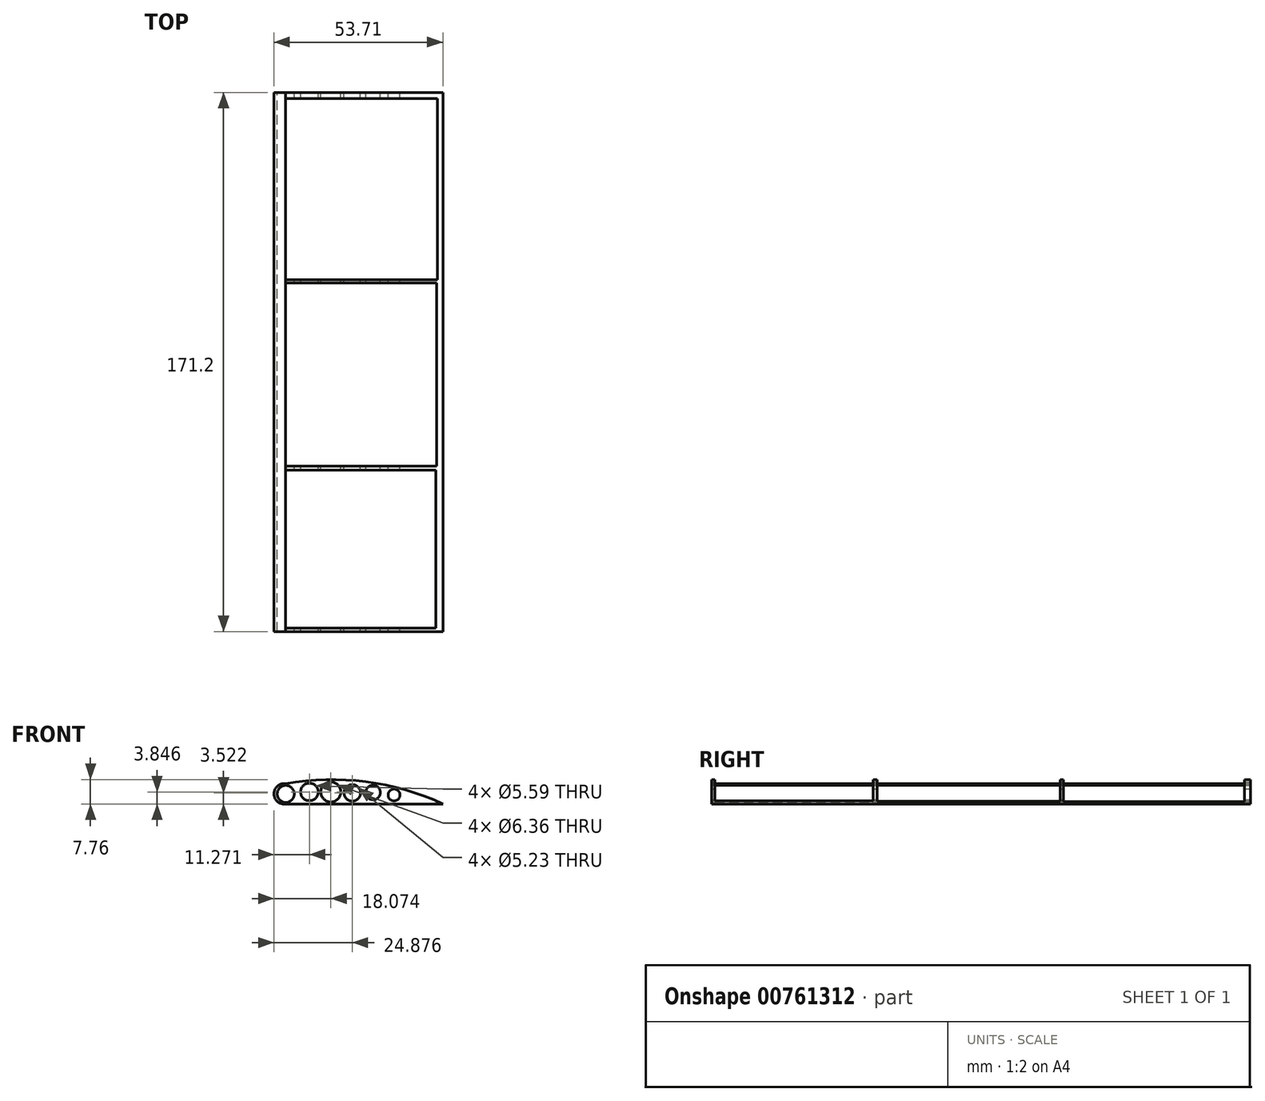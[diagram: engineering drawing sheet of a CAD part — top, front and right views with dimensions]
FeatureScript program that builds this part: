
annotation { "Feature Type Name" : "Feature", "Feature Type Description" : "" }
export const myFeature = defineFeature(function(context is Context, id is Id, definition is map)
    precondition{}
    {
        {
            var Q0;
            Q0=qCreatedBy(makeId("Front.planeOp"),FACE);
            var sketch = newSketch(context, id + "F0", { "sketchPlane" : qUnion([Q0])});
            skArc(sketch, "E0", {"start": v(0, 6.4) * mm, "mid": v(-3.74, 3.2) * mm, "end": v(0, 0) * mm});
            skArc(sketch, "E1", {"start": v(49.97, 0) * mm, "mid": v(25.48, 7.04) * mm, "end": v(0, 6.4) * mm});
            skLineSegment(sketch, "E2", {"start": v(0, 0) * mm, "end": v(49.97, 0) * mm});
            skSolve(sketch);
        }
        {
            var Q0;
            Q0 = qSketchRegion(id + "F0", true);
            extrude(context, id + "F1", {"entities" : qUnion([Q0]), "depth" : 171.2 * mm, "offsetDistance" : 25.4 * mm});
        }
        {
            var Q0;
            Q0=qCreatedBy(makeId("Top.planeOp"),FACE);
            cPlane(context, id + "F2", {"entities" : qUnion([Q0]), "cplaneType" : CPlaneType.OFFSET, "offset" : 75.7 * mm, "oppositeDirection" : true, "width" : 152.4 * mm, "height" : 152.4 * mm});
        }
        {
            var Q0;
            Q0=qCreatedBy(id+"F2.planeOp",FACE);
            var sketch = newSketch(context, id + "F3", { "sketchPlane" : qUnion([Q0])});
            skLineSegment(sketch, "E3.bottom", {"start": v(47.72, -170.15) * mm, "end": v(0, -170.15) * mm});
            skLineSegment(sketch, "E3.top", {"start": v(47.72, -119.94) * mm, "end": v(0, -119.94) * mm});
            skLineSegment(sketch, "E3.left", {"start": v(47.72, -170.15) * mm, "end": v(47.72, -119.94) * mm});
            skLineSegment(sketch, "E3.right", {"start": v(0, -170.15) * mm, "end": v(0, -119.94) * mm});
            skSolve(sketch);
        }
        {
            var Q0;
            Q0 = qSketchRegion(id + "F3", true);
            extrude(context, id + "F4", {"entities" : qUnion([Q0]), "operationType" : NewBodyOperationType.REMOVE, "depth" : 198.12 * mm, "offsetDistance" : 25.4 * mm});
        }
        {
            var Q0;
            Q0=qCreatedBy(makeId("Front.planeOp"),FACE);
            var sketch = newSketch(context, id + "F5", { "sketchPlane" : qUnion([Q0])});
            skCircle(sketch, "E4", {"center": v(0, 3.16) * mm, "radius": 2.7 * mm});
            skSolve(sketch);
        }
        {
            var Q0;
            Q0 = qSketchRegion(id + "F5", true);
            extrude(context, id + "F6", {"entities" : qUnion([Q0]), "operationType" : NewBodyOperationType.REMOVE, "depth" : 205.23 * mm, "offsetDistance" : 25.4 * mm});
        }
        {
            var Q0;
            Q0=qCreatedBy(makeId("Front.planeOp"),FACE);
            var sketch = newSketch(context, id + "F7", { "sketchPlane" : qUnion([Q0])});
            skCircle(sketch, "E5", {"center": v(34.42, 2.83) * mm, "radius": 1.89 * mm});
            skSolve(sketch);
        }
        {
            var Q0;
            Q0 = qSketchRegion(id + "F7", true);
            extrude(context, id + "F8", {"entities" : qUnion([Q0]), "operationType" : NewBodyOperationType.REMOVE, "depth" : 241.05 * mm, "offsetDistance" : 25.4 * mm});
        }
        {
            var Q0;
            Q0=qCreatedBy(makeId("Front.planeOp"),FACE);
            var sketch = newSketch(context, id + "F9", { "sketchPlane" : qUnion([Q0])});
            skCircle(sketch, "E6", {"center": v(7.53, 3.8) * mm, "radius": 2.8 * mm});
            skSolve(sketch);
        }
        {
            var Q0;
            Q0 = qSketchRegion(id + "F9", true);
            extrude(context, id + "F10", {"entities" : qUnion([Q0]), "operationType" : NewBodyOperationType.REMOVE, "depth" : 243.84 * mm, "offsetDistance" : 25.4 * mm});
        }
        {
            var Q0;
            Q0=qCreatedBy(makeId("Front.planeOp"),FACE);
            var sketch = newSketch(context, id + "F11", { "sketchPlane" : qUnion([Q0])});
            skCircle(sketch, "E7", {"center": v(14.33, 3.8) * mm, "radius": 3.18 * mm});
            skSolve(sketch);
        }
        {
            var Q0;
            Q0 = qSketchRegion(id + "F11", true);
            extrude(context, id + "F12", {"entities" : qUnion([Q0]), "operationType" : NewBodyOperationType.REMOVE, "depth" : 208.53 * mm, "offsetDistance" : 25.4 * mm});
        }
        {
            var Q0;
            Q0=qCreatedBy(makeId("Front.planeOp"),FACE);
            var sketch = newSketch(context, id + "F13", { "sketchPlane" : qUnion([Q0])});
            skCircle(sketch, "E8", {"center": v(21.14, 3.48) * mm, "radius": 2.62 * mm});
            skSolve(sketch);
        }
        {
            var Q0;
            Q0 = qSketchRegion(id + "F13", true);
            extrude(context, id + "F14", {"entities" : qUnion([Q0]), "operationType" : NewBodyOperationType.REMOVE, "depth" : 201.42 * mm, "offsetDistance" : 25.4 * mm});
        }
        {
            var Q0;
            Q0=qCreatedBy(makeId("Front.planeOp"),FACE);
            var sketch = newSketch(context, id + "F15", { "sketchPlane" : qUnion([Q0])});
            skCircle(sketch, "E9", {"center": v(27.78, 3.64) * mm, "radius": 2.3 * mm});
            skSolve(sketch);
        }
        {
            var Q0;
            Q0 = qSketchRegion(id + "F15", true);
            extrude(context, id + "F16", {"entities" : qUnion([Q0]), "operationType" : NewBodyOperationType.REMOVE, "depth" : 190.75 * mm, "offsetDistance" : 25.4 * mm});
        }
        {
            var Q0;
            Q0=qCreatedBy(id+"F2.planeOp",FACE);
            var sketch = newSketch(context, id + "F17", { "sketchPlane" : qUnion([Q0])});
            skLineSegment(sketch, "E10.bottom", {"start": v(0, -118.62) * mm, "end": v(47.98, -118.62) * mm});
            skLineSegment(sketch, "E10.top", {"start": v(0, -60.51) * mm, "end": v(47.98, -60.51) * mm});
            skLineSegment(sketch, "E10.left", {"start": v(0, -118.62) * mm, "end": v(0, -60.51) * mm});
            skLineSegment(sketch, "E10.right", {"start": v(47.98, -118.62) * mm, "end": v(47.98, -60.51) * mm});
            skSolve(sketch);
        }
        {
            var Q0;
            Q0 = qSketchRegion(id + "F17", true);
            extrude(context, id + "F18", {"entities" : qUnion([Q0]), "operationType" : NewBodyOperationType.REMOVE, "depth" : 171.2 * mm, "offsetDistance" : 25.4 * mm});
        }
        {
            var Q0;
            Q0=qCreatedBy(id+"F2.planeOp",FACE);
            var sketch = newSketch(context, id + "F19", { "sketchPlane" : qUnion([Q0])});
            skLineSegment(sketch, "E11.bottom", {"start": v(0, -59.46) * mm, "end": v(48.25, -59.46) * mm});
            skLineSegment(sketch, "E11.top", {"start": v(0, -1.88) * mm, "end": v(48.25, -1.88) * mm});
            skLineSegment(sketch, "E11.left", {"start": v(0, -59.46) * mm, "end": v(0, -1.88) * mm});
            skLineSegment(sketch, "E11.right", {"start": v(48.25, -59.46) * mm, "end": v(48.25, -1.88) * mm});
            skSolve(sketch);
        }
        {
            var Q0;
            Q0 = qSketchRegion(id + "F19", true);
            extrude(context, id + "F20", {"entities" : qUnion([Q0]), "operationType" : NewBodyOperationType.REMOVE, "depth" : 182.63 * mm, "offsetDistance" : 25.4 * mm});
        }
    });
